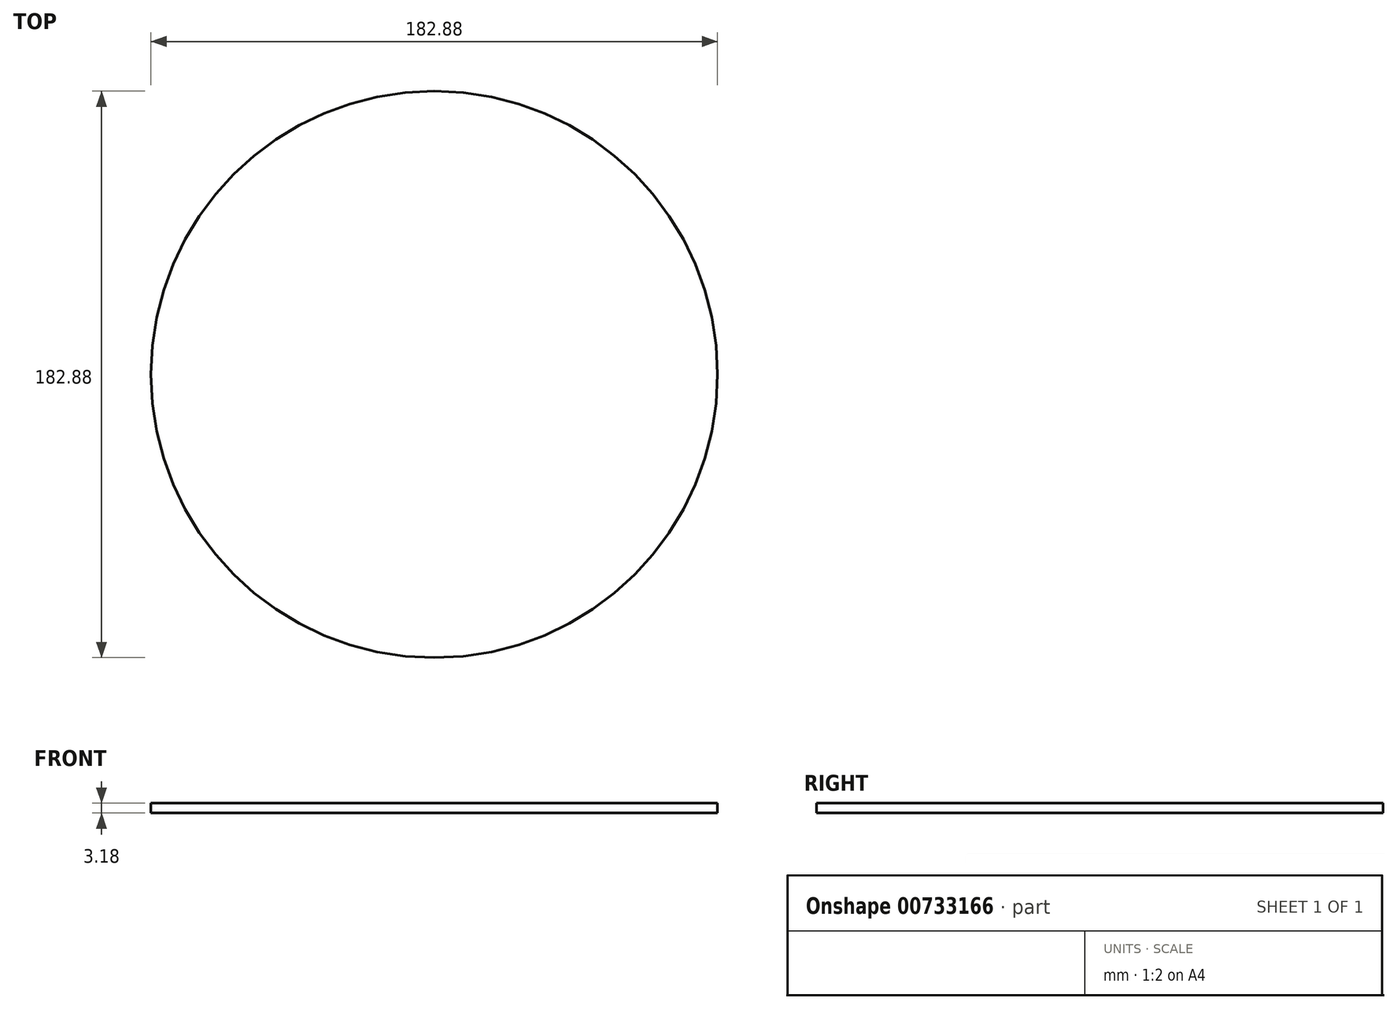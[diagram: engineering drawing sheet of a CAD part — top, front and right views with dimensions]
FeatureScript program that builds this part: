
annotation { "Feature Type Name" : "Feature", "Feature Type Description" : "" }
export const myFeature = defineFeature(function(context is Context, id is Id, definition is map)
    precondition{}
    {
        {
            var Q0;
            Q0=qCreatedBy(makeId("Top.planeOp"),FACE);
            var sketch = newSketch(context, id + "F0", { "sketchPlane" : qUnion([Q0])});
            skCircle(sketch, "E0", {"center": v(0, 0) * mm, "radius": 91.44 * mm});
            skSolve(sketch);
        }
        {
            var Q0;
            Q0 = qSketchRegion(id + "F0", true);
            extrude(context, id + "F1", {"entities" : qUnion([Q0]), "depth" : 3.17 * mm, "offsetDistance" : 25.4 * mm});
        }
    });
